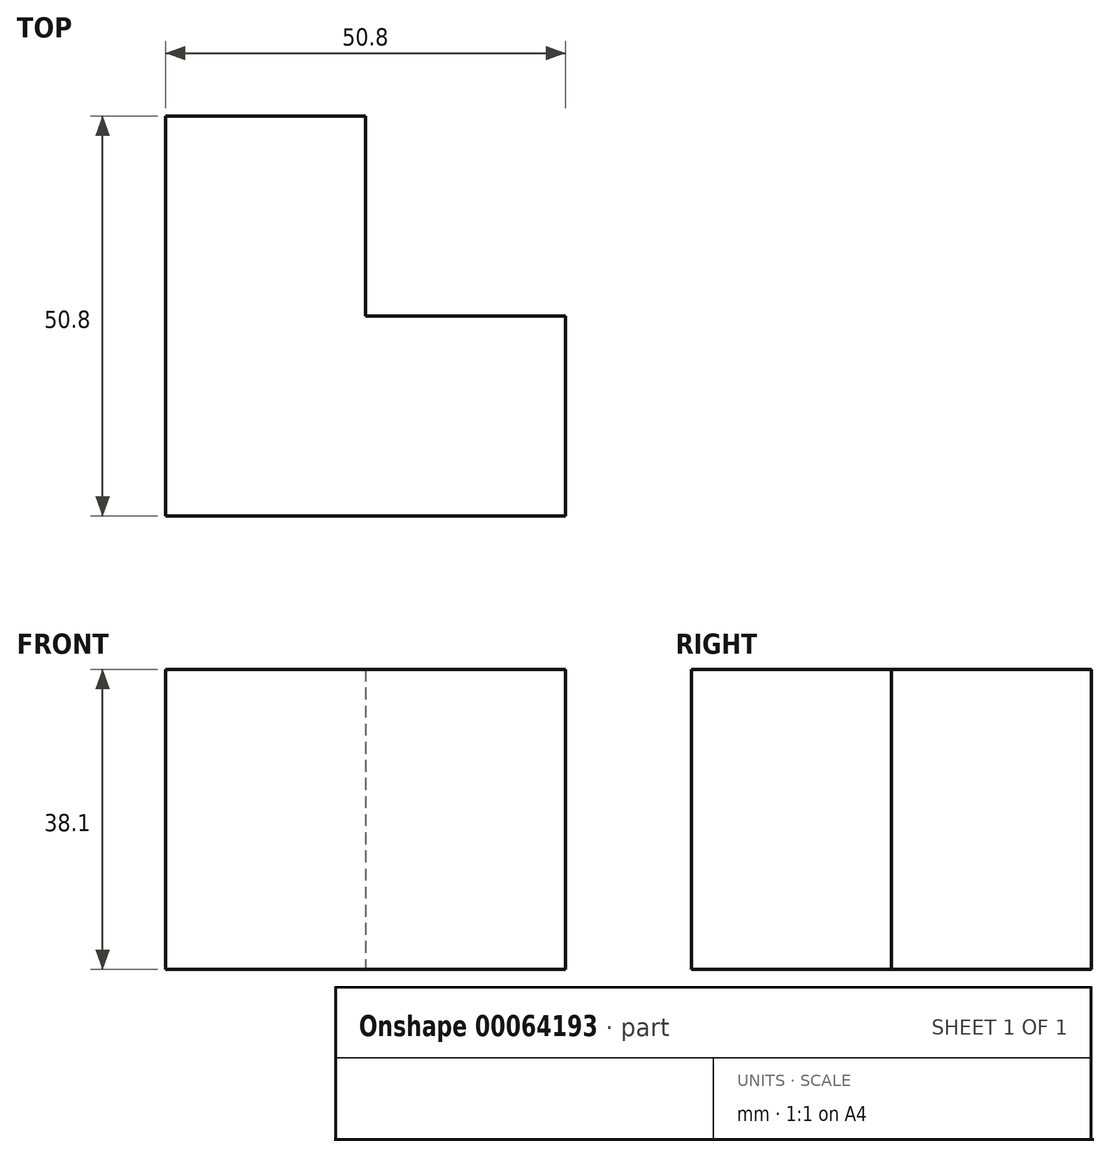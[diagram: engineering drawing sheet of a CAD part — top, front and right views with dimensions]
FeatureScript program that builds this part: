
annotation { "Feature Type Name" : "Feature", "Feature Type Description" : "" }
export const myFeature = defineFeature(function(context is Context, id is Id, definition is map)
    precondition{}
    {
        {
            var Q0;
            Q0=qCreatedBy(makeId("Front.planeOp"),FACE);
            var sketch = newSketch(context, id + "F0", { "sketchPlane" : qUnion([Q0])});
            skLineSegment(sketch, "E0.rect.bottom", {"start": v(25.4, -19.05) * mm, "end": v(-25.4, -19.05) * mm});
            skLineSegment(sketch, "E0.rect.top", {"start": v(25.4, 19.05) * mm, "end": v(-25.4, 19.05) * mm});
            skLineSegment(sketch, "E0.rect.left", {"start": v(25.4, -19.05) * mm, "end": v(25.4, 19.05) * mm});
            skLineSegment(sketch, "E0.rect.right", {"start": v(-25.4, -19.05) * mm, "end": v(-25.4, 19.05) * mm});
            skPoint(sketch, "E0.rect.middle", {"position": v(0, 0) * mm});
            skSolve(sketch);
        }
        {
            var Q0;
            Q0=makeQuery(id+"F0.imprint","IMPRINT",FACE,{"disambiguationData":[TD([[makeQuery(id+"F0.imprint","IMPRINT",EDGE,{"derivedFrom":sQuery(id+"F0.wireOp",EDGE,"E0.rect.bottom")}),-1.0]])]});
            extrude(context, id + "F1", {"entities" : qUnion([Q0]), "depth" : 25.4 * mm});
        }
        {
            var Q0;
            Q0=makeQuery(id+"F1.opExtrude","CAP_FACE",FACE,{"disambiguationData":[OSD([sQuery(id+"F0.wireOp",EDGE,"E0.rect.bottom"),sQuery(id+"F0.wireOp",EDGE,"E0.rect.top"),sQuery(id+"F0.wireOp",EDGE,"E0.rect.left"),sQuery(id+"F0.wireOp",EDGE,"E0.rect.right")])],"isStart":true});
            var sketch = newSketch(context, id + "F2", { "sketchPlane" : qUnion([Q0])});
            skLineSegment(sketch, "E1", {"start": v(0, 19.05) * mm, "end": v(0, -19.05) * mm});
            skSolve(sketch);
        }
        {
            var Q0;
            {var subQ0=sQuery(id+"F2.wireOp",EDGE,"E1");Q0=makeQuery(id+"F2.imprint","IMPRINT",FACE,{"disambiguationData":[TD([[makeQuery(id+"F2.imprint","IMPRINT",EDGE,{"derivedFrom":subQ0}),1.0]])]});}
            extrude(context, id + "F3", {"entities" : qUnion([Q0]), "operationType" : NewBodyOperationType.ADD, "depth" : 25.4 * mm});
        }
    });
